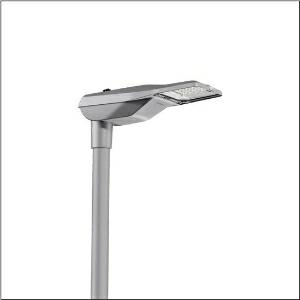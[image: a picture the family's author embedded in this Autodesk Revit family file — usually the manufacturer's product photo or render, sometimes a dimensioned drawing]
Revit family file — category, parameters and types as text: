
# Revit family: streetlight_sl_21_iq_micro___st1_0ab_5xe1m31v08cb_08ed
name_source: partatom
category: Lighting Fixtures
units: mm (PartAtom-declared; Revit-internal decimal feet)

## family parameters
Cut with Voids When Loaded = No
Host = Face
Light Source = No
Part Type = Normal
Room Calculation Point = No
Round Connector Dimension = Use Diameter
Shared = No

## types (1)
- --- (1 x LED, 2530 lm, 19.1 W, 3000K)
    Apparent Load = 19 VA
    CIE Flux Codes = 38 73 97 100 100
    Color Rendering = 70
    Color Temperature = 3000K
    Default Elevation = 1800 mm
    Description = Streetlight SL 21 iQ micro, mast luminaire, primary light control with lens, of PMMA, primary optical cover: cover, of toughened safety glass, transparent, light distribution: ST1.0aB, light emission: direct distribution, primary light characteristic: asymmetric, installation type: post-top, side-entry, LED, High Power LED, rated luminous flux: 2.530lm, luminous efficacy: 133lm/W, light colour: 730, colour temperature: 3000K, control gear: iQ-Street Remote, D4i with power reduction, control: pre-setting: logarithmic dimming characteristic, Street-Remote, Auto-Match, Temp-Guard, Lumen-Switch, Night-Set, Smart-Wire, Light-Fading, Desk-Remote (wireless, voltage-free reading and setting of iQ features in the workshop via application-optimized NFC function/RFID function), optimised constant luminous flux control (CLO 2.0), mains connection: 220..240V, AC, 50/60Hz, start of lifetime: 19W, end of service life: 20W, reduction: 9W, luminaire housing, of diecast aluminium, powder-coated, SITECO metallic grey (DB 702S), corrosivity category C5 high according to DIN EN ISO 12944, please order mast flange separately, inclination adjustable: 0°, 5°, 10°, 15°, sealing non-destructively replaceable, multi-level sealing system, length: 528mm, width: 235mm, height: 110mm, mast flange for spigot size: 42mm (side-entry): 5XC10008XM4, 60/48mm (side-entry/post-top): 5XC10108XM2, 76/60mm (side-entry/post-top): 5XC10108XM1, mounting height: 4..8m, Smart Interface above, protection rating (complete): IP66, insulation class (complete): insulation class II (safety insulation), certification: CE, ENEC, ENEC+, VDE, impact resistance: IK10, permissible operating ambient temperature for outdoor applications: -40..+50°C, standard-compliant lighting for roads and squares, packaging unit: 1 piece

Light Distribution: ST1.0aB
    Height = 110 mm
    Lamp = 1 x LED
    Lamp Light Flux = 2530 lm
    Lamp Power = 19.1 W
    Lamp count = 1
    Length = 528 mm
    Luminous efficacy = 132 lm/W
    Manufacturer = Siteco
    ModVariant = No
    Model = 5XE1M31V08CB
    Number of Poles = 1
    OnlyDefault = Yes
    Power Factor = 1
    Product Name = Streetlight SL 21 iQ micro | ST1.0aB
    Product group = mast luminaire | pylon top
    ProductGroupID = 6100
    Protection Class = Protection class II
    Protection Degree = IP 66
    RLX_Detail_Level = 1
    RLX_Emergency_Light_Flux = 0 lm
    RLX_Emergency_Type = 0
    RLX_Emergency_Type_DB = No
    RlxData = <blob elided: 98345 chars, md5=134c601d>
    Socket = socket
    Standby Power = 0 W
    System Light Flux = 2530 lm
    System Power = 19 W
    Type Comments = factory setting: luminous flux: 100 % | dim-lin: 254 | 387 mA
    Type Image = l_1277292.jpg
    URL = http://relux.com
    VarID = @adj_112739
    Voltage = 0 V
    Weight = 0.00 kg
    Width = 235 mm

## geometry (parser evidence)
native form markers: Blend x4, Sweep x11
no freeform markers — native parametric forms only
